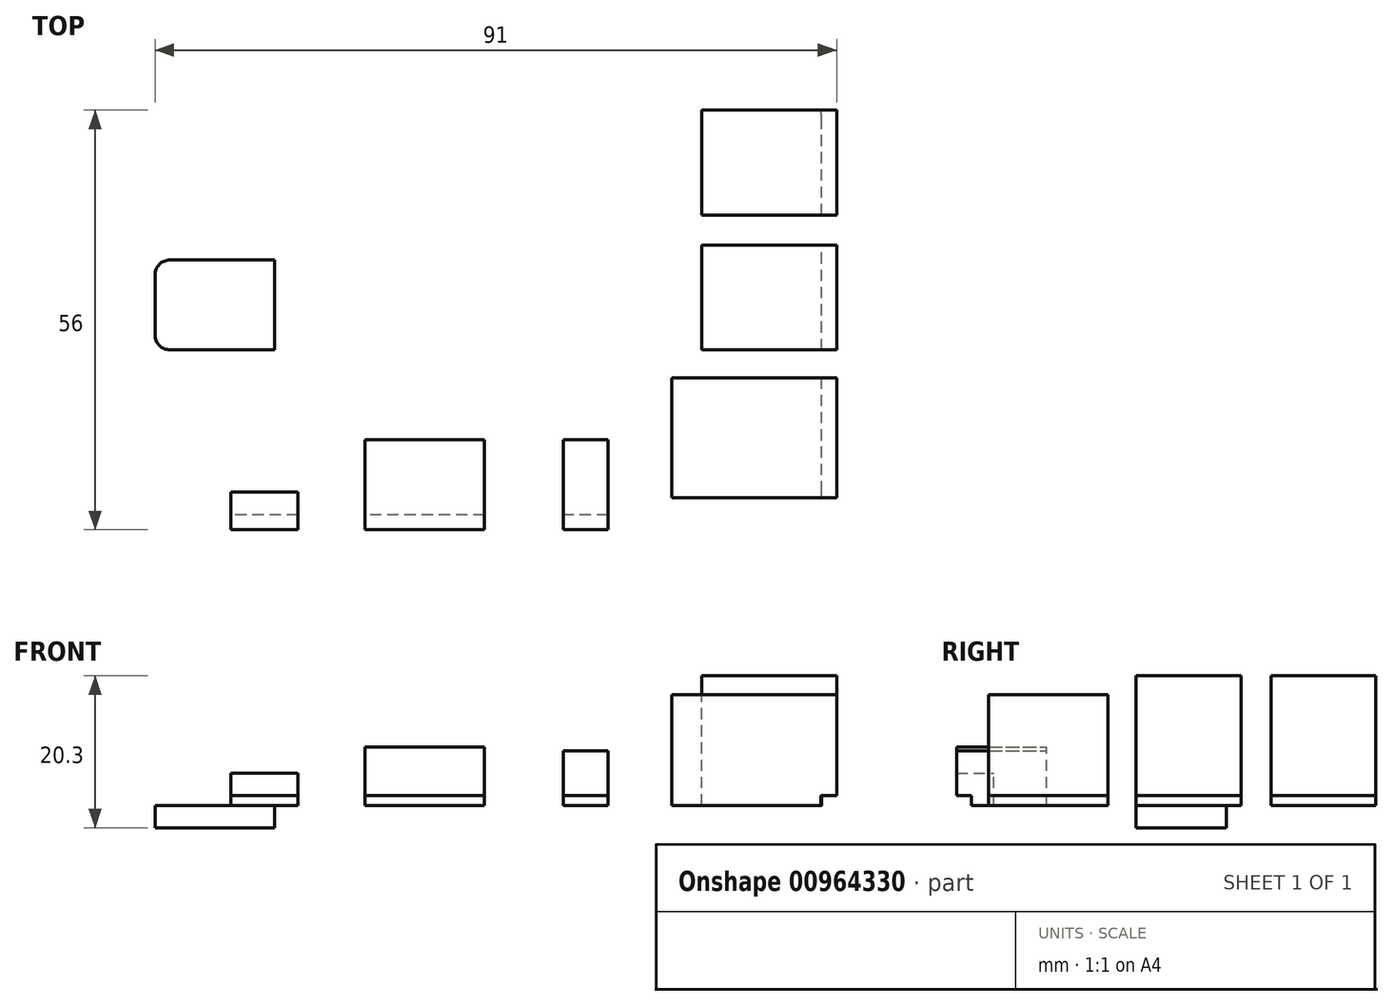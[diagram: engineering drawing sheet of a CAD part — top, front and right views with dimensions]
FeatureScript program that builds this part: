
annotation { "Feature Type Name" : "Feature", "Feature Type Description" : "" }
export const myFeature = defineFeature(function(context is Context, id is Id, definition is map)
    precondition{}
    {
        {
            var Q0;
            Q0=qCreatedBy(makeId("Top.planeOp"),FACE);
            var sketch = newSketch(context, id + "F0", { "sketchPlane" : qUnion([Q0])});
            skLineSegment(sketch, "E0.bottom", {"start": v(-3, 0) * mm, "end": v(-82, 0) * mm});
            skLineSegment(sketch, "E0.top", {"start": v(-3, 56) * mm, "end": v(-82, 56) * mm});
            skLineSegment(sketch, "E0.left", {"start": v(0, 3) * mm, "end": v(0, 53) * mm});
            skLineSegment(sketch, "E0.right", {"start": v(-85, 3) * mm, "end": v(-85, 53) * mm});
            skPoint(sketch, "E1.visualSharp", {"position": v(-85, 56) * mm});
            skArc(sketch, "E1.filletArc", {"start": v(-82, 56) * mm, "mid": v(-84.12, 55.12) * mm, "end": v(-85, 53) * mm});
            skPoint(sketch, "E2.visualSharp", {"position": v(0, 56) * mm});
            skArc(sketch, "E2.filletArc", {"start": v(0, 53) * mm, "mid": v(-0.88, 55.12) * mm, "end": v(-3, 56) * mm});
            skPoint(sketch, "E3.visualSharp", {"position": v(0, 0) * mm});
            skArc(sketch, "E3.filletArc", {"start": v(-3, 0) * mm, "mid": v(-0.88, 0.88) * mm, "end": v(0, 3) * mm});
            skPoint(sketch, "E4.visualSharp", {"position": v(-85, 0) * mm});
            skArc(sketch, "E4.filletArc", {"start": v(-85, 3) * mm, "mid": v(-84.12, 0.88) * mm, "end": v(-82, 0) * mm});
            skLineSegment(sketch, "E5.bottom", {"start": v(-81.5, 52.5) * mm, "end": v(-23.5, 52.5) * mm, "construction": true});
            skLineSegment(sketch, "E5.top", {"start": v(-81.5, 3.5) * mm, "end": v(-23.5, 3.5) * mm, "construction": true});
            skLineSegment(sketch, "E5.left", {"start": v(-81.5, 52.5) * mm, "end": v(-81.5, 3.5) * mm, "construction": true});
            skLineSegment(sketch, "E5.right", {"start": v(-23.5, 52.5) * mm, "end": v(-23.5, 3.5) * mm, "construction": true});
            skCircle(sketch, "E6", {"center": v(-81.5, 52.5) * mm, "radius": 3.5 * mm, "construction": true});
            skCircle(sketch, "E7", {"center": v(-81.5, 52.5) * mm, "radius": 1.38 * mm});
            skLineSegment(sketch, "E8.bottom", {"start": v(-22.12, 53.87) * mm, "end": v(-82.88, 53.87) * mm, "construction": true});
            skLineSegment(sketch, "E8.top", {"start": v(-22.12, 2.13) * mm, "end": v(-82.87, 2.12) * mm, "construction": true});
            skLineSegment(sketch, "E8.left", {"start": v(-22.12, 53.87) * mm, "end": v(-22.12, 2.12) * mm, "construction": true});
            skLineSegment(sketch, "E8.right", {"start": v(-82.88, 53.87) * mm, "end": v(-82.87, 2.12) * mm, "construction": true});
            skCircle(sketch, "E9", {"center": v(-23.5, 52.5) * mm, "radius": 1.38 * mm});
            skCircle(sketch, "E10", {"center": v(-23.5, 3.5) * mm, "radius": 1.38 * mm});
            skCircle(sketch, "E11", {"center": v(-81.5, 3.5) * mm, "radius": 1.37 * mm});
            skCircle(sketch, "E12", {"center": v(-81.5, 3.5) * mm, "radius": 3.5 * mm, "construction": true});
            skLineSegment(sketch, "E13.bottom", {"start": v(-45, -2) * mm, "end": v(-61, -2) * mm});
            skLineSegment(sketch, "E13.top", {"start": v(-45, 10) * mm, "end": v(-61, 10) * mm});
            skLineSegment(sketch, "E13.left", {"start": v(-45, -2) * mm, "end": v(-45, 10) * mm});
            skLineSegment(sketch, "E13.right", {"start": v(-61, -2) * mm, "end": v(-61, 10) * mm});
            skPoint(sketch, "E13.middle", {"position": v(-53, 4) * mm});
            skLineSegment(sketch, "E14.bottom", {"start": v(-69.9, -2) * mm, "end": v(-78.9, -2) * mm});
            skLineSegment(sketch, "E14.top", {"start": v(-69.9, 3) * mm, "end": v(-78.9, 3) * mm});
            skLineSegment(sketch, "E14.left", {"start": v(-69.9, -2) * mm, "end": v(-69.9, 3) * mm});
            skLineSegment(sketch, "E14.right", {"start": v(-78.9, -2) * mm, "end": v(-78.9, 3) * mm});
            skPoint(sketch, "E14.middle", {"position": v(-74.4, 0.5) * mm});
            skLineSegment(sketch, "E15.bottom", {"start": v(2, 2.25) * mm, "end": v(-20, 2.25) * mm});
            skLineSegment(sketch, "E15.top", {"start": v(2, 18.25) * mm, "end": v(-20, 18.25) * mm});
            skLineSegment(sketch, "E15.left", {"start": v(2, 2.25) * mm, "end": v(2, 18.25) * mm});
            skLineSegment(sketch, "E15.right", {"start": v(-20, 2.25) * mm, "end": v(-20, 18.25) * mm});
            skPoint(sketch, "E15.middle", {"position": v(-9, 10.25) * mm});
            skLineSegment(sketch, "E16.bottom", {"start": v(-28.5, -2) * mm, "end": v(-34.5, -2) * mm});
            skLineSegment(sketch, "E16.top", {"start": v(-28.5, 10) * mm, "end": v(-34.5, 10) * mm});
            skLineSegment(sketch, "E16.left", {"start": v(-28.5, -2) * mm, "end": v(-28.5, 10) * mm});
            skLineSegment(sketch, "E16.right", {"start": v(-34.5, -2) * mm, "end": v(-34.5, 10) * mm});
            skPoint(sketch, "E16.middle", {"position": v(-31.5, 4) * mm});
            skLineSegment(sketch, "E17.bottom", {"start": v(2, 22) * mm, "end": v(-16, 22) * mm});
            skLineSegment(sketch, "E17.top", {"start": v(2, 36) * mm, "end": v(-16, 36) * mm});
            skLineSegment(sketch, "E17.left", {"start": v(2, 22) * mm, "end": v(2, 36) * mm});
            skLineSegment(sketch, "E17.right", {"start": v(-16, 22) * mm, "end": v(-16, 36) * mm});
            skPoint(sketch, "E17.middle", {"position": v(-7, 29) * mm});
            skLineSegment(sketch, "E18.bottom", {"start": v(2, 40) * mm, "end": v(-16, 40) * mm});
            skLineSegment(sketch, "E18.top", {"start": v(2, 54) * mm, "end": v(-16, 54) * mm});
            skLineSegment(sketch, "E18.left", {"start": v(2, 40) * mm, "end": v(2, 54) * mm});
            skLineSegment(sketch, "E18.right", {"start": v(-16, 40) * mm, "end": v(-16, 54) * mm});
            skPoint(sketch, "E18.middle", {"position": v(-7, 47) * mm});
            skPoint(sketch, "E19.middle", {"position": v(-85, 28) * mm});
            skSolve(sketch);
        }
        {
            var Q0;
            {var subQ12=sQuery(id+"F0.wireOp",EDGE,"E0.top");Q0=makeQuery(id+"F0.imprint","IMPRINT",FACE,{"disambiguationData":[TD([[makeQuery(id+"F0.imprint","IMPRINT",EDGE,{"derivedFrom":subQ12}),1.0]])]});}
            var Q1;
            {var subQ5=sQuery(id+"F0.wireOp",EDGE,"E14.top");Q1=makeQuery(id+"F0.imprint","IMPRINT",FACE,{"disambiguationData":[TD([[makeQuery(id+"F0.imprint","IMPRINT",EDGE,{"derivedFrom":subQ5}),1.0]])]});}
            var Q2;
            {var subQ5=sQuery(id+"F0.wireOp",EDGE,"E13.top");Q2=makeQuery(id+"F0.imprint","IMPRINT",FACE,{"disambiguationData":[TD([[makeQuery(id+"F0.imprint","IMPRINT",EDGE,{"derivedFrom":subQ5}),1.0]])]});}
            var Q3;
            {var subQ5=sQuery(id+"F0.wireOp",EDGE,"E16.top");Q3=makeQuery(id+"F0.imprint","IMPRINT",FACE,{"disambiguationData":[TD([[makeQuery(id+"F0.imprint","IMPRINT",EDGE,{"derivedFrom":subQ5}),1.0]])]});}
            var Q4;
            {var subQ3=sQuery(id+"F0.wireOp",EDGE,"E15.right");Q4=makeQuery(id+"F0.imprint","IMPRINT",FACE,{"disambiguationData":[TD([[makeQuery(id+"F0.imprint","IMPRINT",EDGE,{"derivedFrom":subQ3}),-1.0]])]});}
            var Q5;
            {var subQ5=sQuery(id+"F0.wireOp",EDGE,"E17.right");Q5=makeQuery(id+"F0.imprint","IMPRINT",FACE,{"disambiguationData":[TD([[makeQuery(id+"F0.imprint","IMPRINT",EDGE,{"derivedFrom":subQ5}),-1.0]])]});}
            var Q6;
            {var subQ3=sQuery(id+"F0.wireOp",EDGE,"E18.right");Q6=makeQuery(id+"F0.imprint","IMPRINT",FACE,{"disambiguationData":[TD([[makeQuery(id+"F0.imprint","IMPRINT",EDGE,{"derivedFrom":subQ3}),-1.0]])]});}
            var Q7;
            {var subQ5=sQuery(id+"F0.wireOp",EDGE,"E19.left");Q7=makeQuery(id+"F0.imprint","IMPRINT",FACE,{"disambiguationData":[TD([[makeQuery(id+"F0.imprint","IMPRINT",EDGE,{"derivedFrom":subQ5}),1.0]])]});}
            extrude(context, id + "F1", {"entities" : qUnion([Q0, Q1, Q2, Q3, Q4, Q5, Q6, Q7]), "oppositeDirection" : true, "depth" : 1.3 * mm, "offsetDistance" : 25 * mm});
        }
        {
            var Q0;
            {var subQ3=sQuery(id+"F0.wireOp",EDGE,"E18.right");Q0=makeQuery(id+"F0.imprint","IMPRINT",FACE,{"disambiguationData":[TD([[makeQuery(id+"F0.imprint","IMPRINT",EDGE,{"derivedFrom":subQ3}),-1.0]])]});}
            var Q1;
            {var subQ5=sQuery(id+"F0.wireOp",EDGE,"E17.right");Q1=makeQuery(id+"F0.imprint","IMPRINT",FACE,{"disambiguationData":[TD([[makeQuery(id+"F0.imprint","IMPRINT",EDGE,{"derivedFrom":subQ5}),-1.0]])]});}
            var Q2;
            {var subQ5=sQuery(id+"F0.wireOp",EDGE,"E17.left");Q2=makeQuery(id+"F0.imprint","IMPRINT",FACE,{"disambiguationData":[TD([[makeQuery(id+"F0.imprint","IMPRINT",EDGE,{"derivedFrom":subQ5}),1.0]])]});}
            var Q3;
            {var subQ3=sQuery(id+"F0.wireOp",EDGE,"E18.left");Q3=makeQuery(id+"F0.imprint","IMPRINT",FACE,{"disambiguationData":[TD([[makeQuery(id+"F0.imprint","IMPRINT",EDGE,{"derivedFrom":subQ3}),1.0]])]});}
            extrude(context, id + "F2", {"entities" : qUnion([Q0, Q1, Q2, Q3]), "operationType" : NewBodyOperationType.ADD, "depth" : 16 * mm, "offsetDistance" : 25 * mm});
        }
        {
            var Q0;
            {var subQ3=sQuery(id+"F0.wireOp",EDGE,"E15.right");Q0=makeQuery(id+"F0.imprint","IMPRINT",FACE,{"disambiguationData":[TD([[makeQuery(id+"F0.imprint","IMPRINT",EDGE,{"derivedFrom":subQ3}),-1.0]])]});}
            var Q1;
            {var subQ3=sQuery(id+"F0.wireOp",EDGE,"E15.left");Q1=makeQuery(id+"F0.imprint","IMPRINT",FACE,{"disambiguationData":[TD([[makeQuery(id+"F0.imprint","IMPRINT",EDGE,{"derivedFrom":subQ3}),1.0]])]});}
            extrude(context, id + "F3", {"entities" : qUnion([Q0, Q1]), "operationType" : NewBodyOperationType.ADD, "depth" : 13.5 * mm, "offsetDistance" : 25 * mm});
        }
        {
            var Q0;
            {var subQ5=sQuery(id+"F0.wireOp",EDGE,"E16.bottom");Q0=makeQuery(id+"F0.imprint","IMPRINT",FACE,{"disambiguationData":[TD([[makeQuery(id+"F0.imprint","IMPRINT",EDGE,{"derivedFrom":subQ5}),-1.0]])]});}
            var Q1;
            {var subQ5=sQuery(id+"F0.wireOp",EDGE,"E16.top");Q1=makeQuery(id+"F0.imprint","IMPRINT",FACE,{"disambiguationData":[TD([[makeQuery(id+"F0.imprint","IMPRINT",EDGE,{"derivedFrom":subQ5}),1.0]])]});}
            extrude(context, id + "F4", {"entities" : qUnion([Q0, Q1]), "operationType" : NewBodyOperationType.ADD, "depth" : 6 * mm, "offsetDistance" : 25 * mm});
        }
        {
            var Q0;
            {var subQ5=sQuery(id+"F0.wireOp",EDGE,"E13.top");Q0=makeQuery(id+"F0.imprint","IMPRINT",FACE,{"disambiguationData":[TD([[makeQuery(id+"F0.imprint","IMPRINT",EDGE,{"derivedFrom":subQ5}),1.0]])]});}
            var Q1;
            {var subQ5=sQuery(id+"F0.wireOp",EDGE,"E13.bottom");Q1=makeQuery(id+"F0.imprint","IMPRINT",FACE,{"disambiguationData":[TD([[makeQuery(id+"F0.imprint","IMPRINT",EDGE,{"derivedFrom":subQ5}),-1.0]])]});}
            extrude(context, id + "F5", {"entities" : qUnion([Q0, Q1]), "operationType" : NewBodyOperationType.ADD, "depth" : 6.5 * mm, "offsetDistance" : 25 * mm});
        }
        {
            var Q0;
            {var subQ5=sQuery(id+"F0.wireOp",EDGE,"E14.top");Q0=makeQuery(id+"F0.imprint","IMPRINT",FACE,{"disambiguationData":[TD([[makeQuery(id+"F0.imprint","IMPRINT",EDGE,{"derivedFrom":subQ5}),1.0]])]});}
            var Q1;
            {var subQ5=sQuery(id+"F0.wireOp",EDGE,"E14.bottom");Q1=makeQuery(id+"F0.imprint","IMPRINT",FACE,{"disambiguationData":[TD([[makeQuery(id+"F0.imprint","IMPRINT",EDGE,{"derivedFrom":subQ5}),-1.0]])]});}
            extrude(context, id + "F6", {"entities" : qUnion([Q0, Q1]), "operationType" : NewBodyOperationType.ADD, "depth" : 3 * mm, "offsetDistance" : 25 * mm});
        }
        {
            var Q0;
            Q0=makeQuery(id+"F1.opExtrude","CAP_FACE",FACE,{"disambiguationData":[OSD([sQuery(id+"F0.wireOp",EDGE,"E0.bottom"),sQuery(id+"F0.wireOp",EDGE,"E0.top"),sQuery(id+"F0.wireOp",EDGE,"E0.left"),sQuery(id+"F0.wireOp",EDGE,"E0.right"),sQuery(id+"F0.wireOp",EDGE,"E1.filletArc"),sQuery(id+"F0.wireOp",EDGE,"E2.filletArc"),sQuery(id+"F0.wireOp",EDGE,"E3.filletArc"),sQuery(id+"F0.wireOp",EDGE,"E4.filletArc"),sQuery(id+"F0.wireOp",EDGE,"E7"),sQuery(id+"F0.wireOp",EDGE,"E9"),sQuery(id+"F0.wireOp",EDGE,"E10"),sQuery(id+"F0.wireOp",EDGE,"E11")])],"isStart":false});
            var sketch = newSketch(context, id + "F7", { "sketchPlane" : qUnion([Q0])});
            skArc(sketch, "E20.0.0", {"start": v(-82, 0) * mm, "mid": v(-84.12, -0.88) * mm, "end": v(-85, -3) * mm});
            skLineSegment(sketch, "E20.0.1", {"start": v(-85, -3) * mm, "end": v(-85, -53) * mm});
            skArc(sketch, "E20.0.2", {"start": v(-85, -53) * mm, "mid": v(-84.12, -55.12) * mm, "end": v(-82, -56) * mm});
            skLineSegment(sketch, "E20.0.3", {"start": v(-82, -56) * mm, "end": v(-3, -56) * mm});
            skArc(sketch, "E20.0.4", {"start": v(-3, -56) * mm, "mid": v(-0.88, -55.12) * mm, "end": v(0, -53) * mm});
            skLineSegment(sketch, "E20.0.5", {"start": v(0, -53) * mm, "end": v(0, -3) * mm});
            skArc(sketch, "E20.0.6", {"start": v(0, -3) * mm, "mid": v(-0.88, -0.88) * mm, "end": v(-3, 0) * mm});
            skLineSegment(sketch, "E20.0.7", {"start": v(-3, 0) * mm, "end": v(-82, 0) * mm});
            skLineSegment(sketch, "E21", {"start": v(-85, -28) * mm, "end": v(0, -28) * mm, "construction": true});
            skLineSegment(sketch, "E22.bottom", {"start": v(-73, -34) * mm, "end": v(-89, -34) * mm});
            skLineSegment(sketch, "E22.top", {"start": v(-73, -22) * mm, "end": v(-89, -22) * mm});
            skLineSegment(sketch, "E22.left", {"start": v(-73, -34) * mm, "end": v(-73, -22) * mm});
            skLineSegment(sketch, "E22.right", {"start": v(-89, -34) * mm, "end": v(-89, -22) * mm});
            skPoint(sketch, "E22.middle", {"position": v(-81, -28) * mm});
            skSolve(sketch);
        }
        {
            var Q0;
            {var subQ5=sQuery(id+"F7.wireOp",EDGE,"E22.right");Q0=makeQuery(id+"F7.imprint","IMPRINT",FACE,{"disambiguationData":[TD([[makeQuery(id+"F7.imprint","IMPRINT",EDGE,{"derivedFrom":subQ5}),-1.0]])]});}
            var Q1;
            {var subQ5=sQuery(id+"F7.wireOp",EDGE,"E22.left");Q1=makeQuery(id+"F7.imprint","IMPRINT",FACE,{"disambiguationData":[TD([[makeQuery(id+"F7.imprint","IMPRINT",EDGE,{"derivedFrom":subQ5}),1.0]])]});}
            extrude(context, id + "F8", {"entities" : qUnion([Q0, Q1]), "operationType" : NewBodyOperationType.ADD, "depth" : 3 * mm, "offsetDistance" : 25 * mm});
        }
        {
            var Q0;
            Q0=makeQuery(id+"F8.opExtrude","SWEPT_EDGE",EDGE,{"disambiguationData":[OSD([sQuery(id+"F7.wireOp",EDGE,"E22.top"),sQuery(id+"F7.wireOp",EDGE,"E22.right")])]});
            var Q1;
            Q1=makeQuery(id+"F8.opExtrude","SWEPT_EDGE",EDGE,{"disambiguationData":[OSD([sQuery(id+"F7.wireOp",EDGE,"E22.bottom"),sQuery(id+"F7.wireOp",EDGE,"E22.right")])]});
            fillet(context, id + "F9", {"entities" : qUnion([Q0, Q1]), "tangentPropagation" : true, "radius" : 2 * mm, "defaultsChanged" : true, "vertexSettings" : [], "allowEdgeOverflow" : false});
        }
    });
